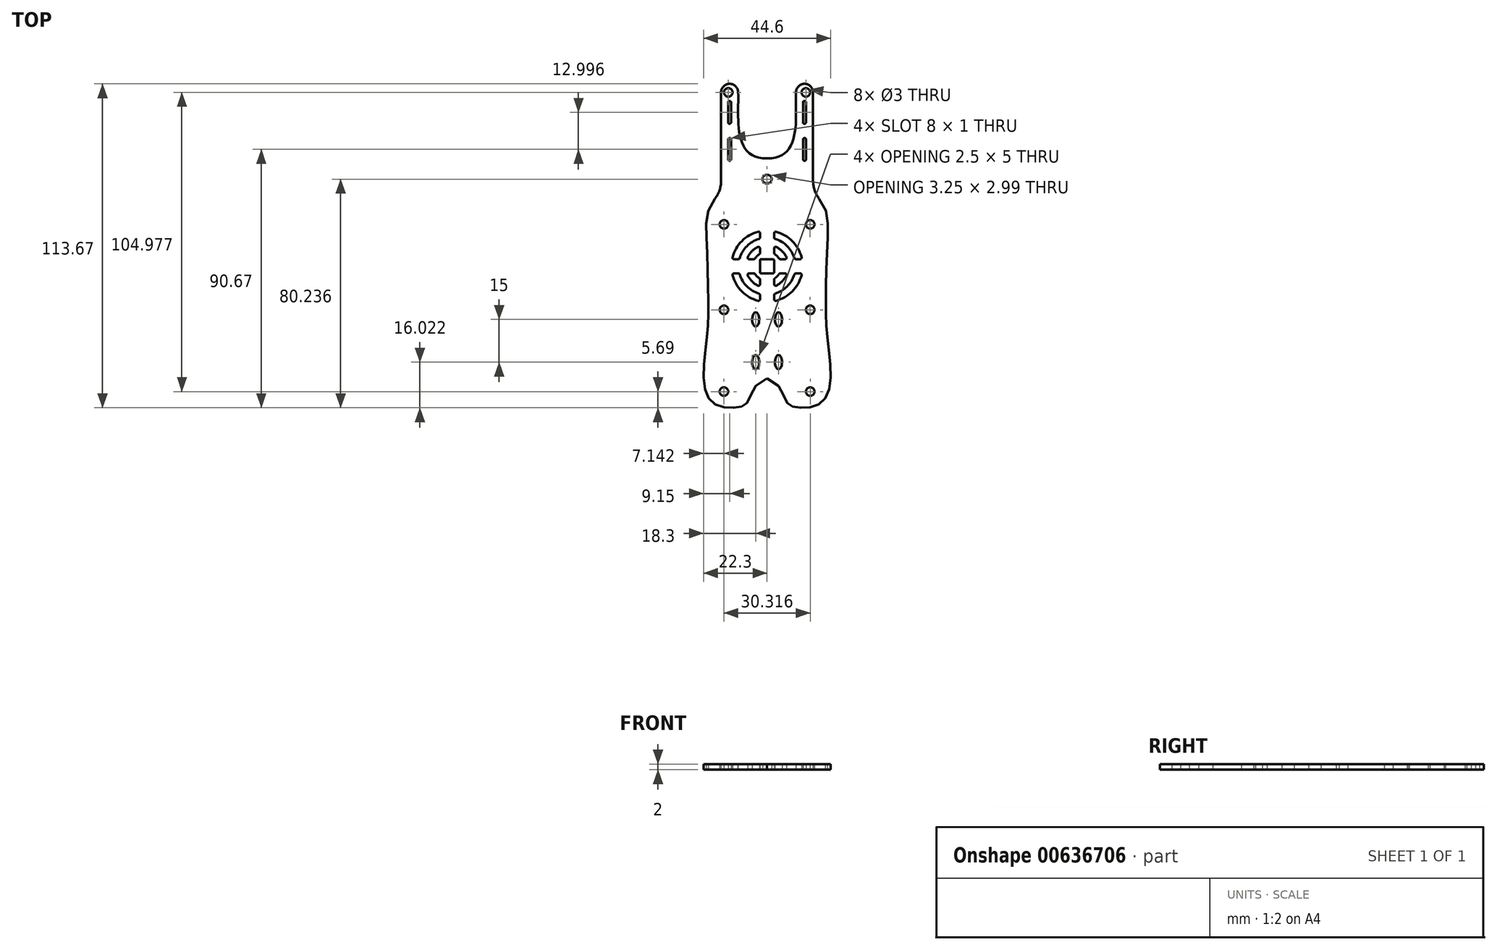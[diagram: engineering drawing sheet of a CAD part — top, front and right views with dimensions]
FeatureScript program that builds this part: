
annotation { "Feature Type Name" : "Feature", "Feature Type Description" : "" }
export const myFeature = defineFeature(function(context is Context, id is Id, definition is map)
    precondition{}
    {
        {
            var Q0;
            Q0=qCreatedBy(makeId("Top.planeOp"),FACE);
            var sketch = newSketch(context, id + "F0", { "sketchPlane" : qUnion([Q0])});
            skCircle(sketch, "E0", {"center": v(15.13, 14.7) * mm, "radius": 1.5 * mm});
            skCircle(sketch, "E1.MirrorC", {"center": v(15.13, -15.3) * mm, "radius": 1.5 * mm});
            skLineSegment(sketch, "E2", {"start": v(16.15, 29.9) * mm, "end": v(16.15, 61) * mm});
            skPoint(sketch, "E3.visualSharp", {"position": v(16.15, 66) * mm});
            skArc(sketch, "E3.filletArc", {"start": v(16.15, 61) * mm, "mid": v(15.24, 63.16) * mm, "end": v(13.06, 64) * mm});
            skArc(sketch, "E4", {"start": v(13.65, 57.5) * mm, "mid": v(13.11, 58) * mm, "end": v(12.65, 57.44) * mm});
            skArc(sketch, "E5", {"start": v(12.65, 37.58) * mm, "mid": v(13.11, 37.01) * mm, "end": v(13.65, 37.5) * mm});
            skLineSegment(sketch, "E6", {"start": v(13.65, 57.5) * mm, "end": v(13.65, 50.5) * mm});
            skLineSegment(sketch, "E7", {"start": v(12.65, 57.57) * mm, "end": v(12.65, 50.44) * mm});
            skPoint(sketch, "E8.visualSharp", {"position": v(8.63, 59.12) * mm});
            skPoint(sketch, "E9.visualSharp", {"position": v(8.63, 31.4) * mm});
            skCircle(sketch, "E10.MirrorC", {"center": v(13.63, 61) * mm, "radius": 1.5 * mm});
            skArc(sketch, "E11", {"start": v(12.65, 50.57) * mm, "mid": v(13.11, 50) * mm, "end": v(13.65, 50.5) * mm});
            skArc(sketch, "E12", {"start": v(13.65, 44.5) * mm, "mid": v(13.11, 45) * mm, "end": v(12.65, 44.44) * mm});
            skLineSegment(sketch, "E13.trimOffspring", {"start": v(12.65, 44.58) * mm, "end": v(12.65, 37.44) * mm});
            skLineSegment(sketch, "E14.trimOffspring", {"start": v(13.65, 44.5) * mm, "end": v(13.65, 37.5) * mm});
            skCircle(sketch, "E15", {"center": v(0.13, 30.58) * mm, "radius": 1.5 * mm});
            skCircle(sketch, "E16", {"center": v(15.16, -43.97) * mm, "radius": 1.5 * mm});
            skArc(sketch, "E17", {"start": v(13.06, 64) * mm, "mid": v(11, 63.1) * mm, "end": v(10.15, 61) * mm});
            skFitSpline(sketch, "E18", {"points": [v(10.15, 61) * mm, v(0, 37.84) * mm], "startDerivative": vector(-1.26, -21.95) * mm, "endDerivative": vector(-37.96, 1.2) * mm});
            skFitSpline(sketch, "E19", {"points": [v(16.15, 26) * mm, v(21.25, 10.3) * mm, v(20.6, -12.8) * mm, v(21.22, -25.83) * mm, v(22.05, -41.9) * mm, v(17.96, -48.52) * mm, v(10.33, -49.5) * mm, v(6.8, -47.51) * mm, v(0, -39.35) * mm], "startDerivative": vector(112.4, -103.66) * mm, "endDerivative": vector(-131.84, 47.57) * mm});
            skArc(sketch, "E20.MirrorCS", {"start": v(-12.65, 37.58) * mm, "mid": v(-13.11, 37.01) * mm, "end": v(-13.65, 37.5) * mm});
            skArc(sketch, "E21.MirrorCS", {"start": v(-12.65, 50.57) * mm, "mid": v(-13.11, 50) * mm, "end": v(-13.65, 50.5) * mm});
            skArc(sketch, "E22.MirrorCS", {"start": v(-13.65, 57.5) * mm, "mid": v(-13.11, 58) * mm, "end": v(-12.65, 57.44) * mm});
            skArc(sketch, "E23.MirrorCS", {"start": v(-13.65, 44.5) * mm, "mid": v(-13.11, 45) * mm, "end": v(-12.65, 44.44) * mm});
            skLineSegment(sketch, "E24.MirrorCS", {"start": v(-13.65, 57.5) * mm, "end": v(-13.65, 50.5) * mm});
            skCircle(sketch, "E25.MirrorC", {"center": v(-13.63, 61) * mm, "radius": 1.5 * mm});
            skLineSegment(sketch, "E26.MirrorCS", {"start": v(-12.65, 57.57) * mm, "end": v(-12.65, 50.44) * mm});
            skArc(sketch, "E27.MirrorCS", {"start": v(-16.15, 61) * mm, "mid": v(-15.24, 63.16) * mm, "end": v(-13.06, 64) * mm});
            skCircle(sketch, "E28.MirrorC", {"center": v(-0.13, 30.58) * mm, "radius": 1.5 * mm});
            skCircle(sketch, "E29.MirrorC", {"center": v(-15.16, -43.97) * mm, "radius": 1.5 * mm});
            skCircle(sketch, "E30.MirrorC", {"center": v(-15.13, -15.3) * mm, "radius": 1.5 * mm});
            skLineSegment(sketch, "E31.MirrorCS", {"start": v(-13.65, 44.5) * mm, "end": v(-13.65, 37.5) * mm});
            skCircle(sketch, "E32.MirrorC", {"center": v(-15.13, 14.7) * mm, "radius": 1.5 * mm});
            skLineSegment(sketch, "E33.MirrorCS", {"start": v(-16.15, 29.9) * mm, "end": v(-16.15, 61) * mm});
            skLineSegment(sketch, "E34.MirrorCS", {"start": v(-12.65, 44.58) * mm, "end": v(-12.65, 37.44) * mm});
            skArc(sketch, "E35.MirrorCS", {"start": v(-13.06, 64) * mm, "mid": v(-11, 63.1) * mm, "end": v(-10.15, 61) * mm});
            skPoint(sketch, "E36.MirrorP", {"position": v(-16.15, 66) * mm});
            skPoint(sketch, "E37.MirrorP", {"position": v(-8.63, 31.4) * mm});
            skFitSpline(sketch, "E38.MirrorCS", {"points": [v(-16.15, 26) * mm, v(-21.25, 10.3) * mm, v(-20.6, -12.8) * mm, v(-21.22, -25.83) * mm, v(-22.05, -41.9) * mm, v(-17.96, -48.52) * mm, v(-10.33, -49.5) * mm, v(-6.8, -47.51) * mm, v(0, -39.35) * mm], "startDerivative": vector(-112.4, -103.66) * mm, "endDerivative": vector(131.84, 47.57) * mm});
            skFitSpline(sketch, "E39.MirrorCS", {"points": [v(-10.15, 61) * mm, v(0, 37.84) * mm], "startDerivative": vector(1.26, -21.95) * mm, "endDerivative": vector(37.96, 1.2) * mm});
            skPoint(sketch, "E40.MirrorP", {"position": v(-8.63, 59.12) * mm});
            skArc(sketch, "E41.filletArc", {"start": v(-18.3, 23.7) * mm, "mid": v(-16.7, 26.62) * mm, "end": v(-16.15, 29.9) * mm});
            skArc(sketch, "E42.filletArc", {"start": v(16.15, 29.9) * mm, "mid": v(16.7, 26.62) * mm, "end": v(18.3, 23.7) * mm});
            skEllipse(sketch, "E43", {"center": v(-4, -33.64) * mm, "majorRadius": 2.5 * mm, "minorRadius": 1.25 * mm, "majorAxis": v(0, -1)});
            skEllipse(sketch, "E44", {"center": v(-4, -18.64) * mm, "majorRadius": 2.5 * mm, "minorRadius": 1.25 * mm, "majorAxis": v(0, -1)});
            skArc(sketch, "E45", {"start": v(-2.72, 4.2) * mm, "mid": v(-3.54, 3.54) * mm, "end": v(-4.2, 2.72) * mm});
            skArc(sketch, "E46", {"start": v(-3.2, 6.78) * mm, "mid": v(-5.3, 5.3) * mm, "end": v(-6.78, 3.2) * mm});
            skArc(sketch, "E47", {"start": v(-2.85, 9.58) * mm, "mid": v(-7.07, 7.07) * mm, "end": v(-9.58, 2.85) * mm});
            skArc(sketch, "E48", {"start": v(-3.12, 12.1) * mm, "mid": v(-8.84, 8.84) * mm, "end": v(-12.1, 3.12) * mm});
            skLineSegment(sketch, "E49.left", {"start": v(2.5, -11.63) * mm, "end": v(2.5, -10.06) * mm});
            skLineSegment(sketch, "E49.right", {"start": v(-2.5, -11.63) * mm, "end": v(-2.5, -10.06) * mm});
            skLineSegment(sketch, "E50.bottom", {"start": v(11.63, -2.5) * mm, "end": v(10.06, -2.5) * mm});
            skLineSegment(sketch, "E50.top", {"start": v(11.63, 2.5) * mm, "end": v(10.06, 2.5) * mm});
            skArc(sketch, "E51.trimOffspring", {"start": v(2.72, -4.2) * mm, "mid": v(3.54, -3.54) * mm, "end": v(4.2, -2.72) * mm});
            skArc(sketch, "E52.trimOffspring", {"start": v(3.2, -6.78) * mm, "mid": v(5.3, -5.3) * mm, "end": v(6.78, -3.2) * mm});
            skArc(sketch, "E53.trimOffspring", {"start": v(2.85, -9.58) * mm, "mid": v(7.07, -7.07) * mm, "end": v(9.58, -2.85) * mm});
            skArc(sketch, "E54.trimOffspring", {"start": v(3.12, -12.1) * mm, "mid": v(8.84, -8.84) * mm, "end": v(12.1, -3.12) * mm});
            skPoint(sketch, "E55.orphan", {"position": v(-17.4, -2.5) * mm});
            skPoint(sketch, "E56.orphan", {"position": v(-17.4, 2.5) * mm});
            skArc(sketch, "E57.trimOffspring", {"start": v(-12.1, -3.12) * mm, "mid": v(-8.84, -8.84) * mm, "end": v(-3.12, -12.1) * mm});
            skArc(sketch, "E58.trimOffspring", {"start": v(-9.58, -2.85) * mm, "mid": v(-7.07, -7.07) * mm, "end": v(-2.85, -9.58) * mm});
            skArc(sketch, "E59.trimOffspring", {"start": v(-6.78, -3.2) * mm, "mid": v(-5.3, -5.3) * mm, "end": v(-3.2, -6.78) * mm});
            skArc(sketch, "E60.trimOffspring", {"start": v(-4.2, -2.72) * mm, "mid": v(-3.54, -3.54) * mm, "end": v(-2.72, -4.2) * mm});
            skLineSegment(sketch, "E61.trimOffspring", {"start": v(-4.6, -2.5) * mm, "end": v(-6.34, -2.5) * mm});
            skLineSegment(sketch, "E62.trimOffspring", {"start": v(-2.5, -2) * mm, "end": v(-2.5, 2) * mm});
            skLineSegment(sketch, "E63.trimOffspring", {"start": v(2.5, -2) * mm, "end": v(2.5, 2) * mm});
            skLineSegment(sketch, "E64.trimOffspring", {"start": v(2, -2.5) * mm, "end": v(-2, -2.5) * mm});
            skLineSegment(sketch, "E65.trimOffspring", {"start": v(2, 2.5) * mm, "end": v(-2, 2.5) * mm});
            skLineSegment(sketch, "E66.trimOffspring", {"start": v(2.5, 4.6) * mm, "end": v(2.5, 6.34) * mm});
            skLineSegment(sketch, "E67.trimOffspring", {"start": v(-2.5, 4.6) * mm, "end": v(-2.5, 6.34) * mm});
            skLineSegment(sketch, "E68.trimOffspring", {"start": v(-4.6, 2.5) * mm, "end": v(-6.34, 2.5) * mm});
            skPoint(sketch, "E69.orphan", {"position": v(-2.5, 16.27) * mm});
            skPoint(sketch, "E70.orphan", {"position": v(2.5, 16.27) * mm});
            skPoint(sketch, "E50.left.end.orphan", {"position": v(17.4, 2.5) * mm});
            skPoint(sketch, "E71.orphan", {"position": v(17.4, -2.5) * mm});
            skPoint(sketch, "E72.orphan", {"position": v(2.5, -16.27) * mm});
            skPoint(sketch, "E73.orphan", {"position": v(-2.5, -16.27) * mm});
            skArc(sketch, "E74.trimOffspring", {"start": v(4.2, 2.72) * mm, "mid": v(3.54, 3.54) * mm, "end": v(2.72, 4.2) * mm});
            skArc(sketch, "E75.trimOffspring", {"start": v(6.78, 3.2) * mm, "mid": v(5.3, 5.3) * mm, "end": v(3.2, 6.78) * mm});
            skArc(sketch, "E76.trimOffspring", {"start": v(9.58, 2.85) * mm, "mid": v(7.07, 7.07) * mm, "end": v(2.85, 9.58) * mm});
            skArc(sketch, "E77.trimOffspring", {"start": v(12.1, 3.12) * mm, "mid": v(8.84, 8.84) * mm, "end": v(3.12, 12.1) * mm});
            skLineSegment(sketch, "E78.trimOffspring", {"start": v(2.5, 10.06) * mm, "end": v(2.5, 11.63) * mm});
            skLineSegment(sketch, "E79.trimOffspring", {"start": v(6.34, 2.5) * mm, "end": v(4.6, 2.5) * mm});
            skLineSegment(sketch, "E80.trimOffspring", {"start": v(-2.5, 10.06) * mm, "end": v(-2.5, 11.63) * mm});
            skLineSegment(sketch, "E81.trimOffspring", {"start": v(-10.06, 2.5) * mm, "end": v(-11.63, 2.5) * mm});
            skLineSegment(sketch, "E82.trimOffspring", {"start": v(-2.5, -6.34) * mm, "end": v(-2.5, -4.6) * mm});
            skLineSegment(sketch, "E83.trimOffspring", {"start": v(2.5, -6.34) * mm, "end": v(2.5, -4.6) * mm});
            skLineSegment(sketch, "E84.trimOffspring", {"start": v(6.34, -2.5) * mm, "end": v(4.6, -2.5) * mm});
            skPoint(sketch, "E85.visualSharp", {"position": v(-9.68, 2.5) * mm});
            skArc(sketch, "E85.filletArc", {"start": v(-10.06, 2.5) * mm, "mid": v(-9.76, 2.6) * mm, "end": v(-9.58, 2.85) * mm});
            skPoint(sketch, "E86.visualSharp", {"position": v(-12.25, 2.5) * mm});
            skArc(sketch, "E86.filletArc", {"start": v(-12.1, 3.12) * mm, "mid": v(-12.02, 2.7) * mm, "end": v(-11.63, 2.5) * mm});
            skPoint(sketch, "E87.visualSharp", {"position": v(-2.5, 12.25) * mm});
            skArc(sketch, "E87.filletArc", {"start": v(-2.5, 11.63) * mm, "mid": v(-2.7, 12.02) * mm, "end": v(-3.12, 12.1) * mm});
            skPoint(sketch, "E88.visualSharp", {"position": v(-2.5, 9.68) * mm});
            skArc(sketch, "E88.filletArc", {"start": v(-2.85, 9.58) * mm, "mid": v(-2.6, 9.76) * mm, "end": v(-2.5, 10.06) * mm});
            skPoint(sketch, "E89.visualSharp", {"position": v(-2.5, 4.33) * mm});
            skArc(sketch, "E89.filletArc", {"start": v(-2.72, 4.2) * mm, "mid": v(-2.56, 4.37) * mm, "end": v(-2.5, 4.6) * mm});
            skPoint(sketch, "E90.visualSharp", {"position": v(-4.33, 2.5) * mm});
            skArc(sketch, "E90.filletArc", {"start": v(-4.6, 2.5) * mm, "mid": v(-4.37, 2.56) * mm, "end": v(-4.2, 2.72) * mm});
            skPoint(sketch, "E91.visualSharp", {"position": v(-7.07, 2.5) * mm});
            skArc(sketch, "E91.filletArc", {"start": v(-6.78, 3.2) * mm, "mid": v(-6.75, 2.73) * mm, "end": v(-6.34, 2.5) * mm});
            skPoint(sketch, "E92.visualSharp", {"position": v(2.5, 12.25) * mm});
            skArc(sketch, "E92.filletArc", {"start": v(3.12, 12.1) * mm, "mid": v(2.7, 12.02) * mm, "end": v(2.5, 11.63) * mm});
            skPoint(sketch, "E93.visualSharp", {"position": v(2.5, 4.33) * mm});
            skArc(sketch, "E93.filletArc", {"start": v(2.5, 4.6) * mm, "mid": v(2.56, 4.37) * mm, "end": v(2.72, 4.2) * mm});
            skPoint(sketch, "E94.visualSharp", {"position": v(2.5, 7.07) * mm});
            skArc(sketch, "E94.filletArc", {"start": v(3.2, 6.78) * mm, "mid": v(2.73, 6.75) * mm, "end": v(2.5, 6.34) * mm});
            skPoint(sketch, "E95.visualSharp", {"position": v(2.5, 9.68) * mm});
            skArc(sketch, "E95.filletArc", {"start": v(2.5, 10.06) * mm, "mid": v(2.6, 9.76) * mm, "end": v(2.85, 9.58) * mm});
            skPoint(sketch, "E96.visualSharp", {"position": v(7.07, 2.5) * mm});
            skArc(sketch, "E96.filletArc", {"start": v(6.34, 2.5) * mm, "mid": v(6.75, 2.73) * mm, "end": v(6.78, 3.2) * mm});
            skPoint(sketch, "E97.visualSharp", {"position": v(9.68, 2.5) * mm});
            skArc(sketch, "E97.filletArc", {"start": v(9.58, 2.85) * mm, "mid": v(9.76, 2.6) * mm, "end": v(10.06, 2.5) * mm});
            skPoint(sketch, "E98.visualSharp", {"position": v(12.25, 2.5) * mm});
            skArc(sketch, "E98.filletArc", {"start": v(11.63, 2.5) * mm, "mid": v(12.02, 2.7) * mm, "end": v(12.1, 3.12) * mm});
            skPoint(sketch, "E99.visualSharp", {"position": v(4.33, 2.5) * mm});
            skArc(sketch, "E99.filletArc", {"start": v(4.2, 2.72) * mm, "mid": v(4.37, 2.56) * mm, "end": v(4.6, 2.5) * mm});
            skPoint(sketch, "E100.visualSharp", {"position": v(4.33, -2.5) * mm});
            skArc(sketch, "E100.filletArc", {"start": v(4.6, -2.5) * mm, "mid": v(4.37, -2.56) * mm, "end": v(4.2, -2.72) * mm});
            skPoint(sketch, "E101.visualSharp", {"position": v(2.5, -2.5) * mm});
            skArc(sketch, "E101.filletArc", {"start": v(2, -2.5) * mm, "mid": v(2.36, -2.36) * mm, "end": v(2.5, -2) * mm});
            skPoint(sketch, "E102.visualSharp", {"position": v(-2.5, -2.5) * mm});
            skArc(sketch, "E102.filletArc", {"start": v(-2.5, -2) * mm, "mid": v(-2.36, -2.36) * mm, "end": v(-2, -2.5) * mm});
            skPoint(sketch, "E103.visualSharp", {"position": v(2.5, 2.5) * mm});
            skArc(sketch, "E103.filletArc", {"start": v(2.5, 2) * mm, "mid": v(2.36, 2.36) * mm, "end": v(2, 2.5) * mm});
            skPoint(sketch, "E104.visualSharp", {"position": v(-4.33, -2.5) * mm});
            skArc(sketch, "E104.filletArc", {"start": v(-4.2, -2.72) * mm, "mid": v(-4.37, -2.56) * mm, "end": v(-4.6, -2.5) * mm});
            skPoint(sketch, "E105.visualSharp", {"position": v(-2.5, -7.07) * mm});
            skArc(sketch, "E105.filletArc", {"start": v(-3.2, -6.78) * mm, "mid": v(-2.73, -6.75) * mm, "end": v(-2.5, -6.34) * mm});
            skLineSegment(sketch, "E106.trimOffspring", {"start": v(-10.06, -2.5) * mm, "end": v(-11.63, -2.5) * mm});
            skPoint(sketch, "E107.visualSharp", {"position": v(-7.07, -2.5) * mm});
            skArc(sketch, "E107.filletArc", {"start": v(-6.34, -2.5) * mm, "mid": v(-6.75, -2.73) * mm, "end": v(-6.78, -3.2) * mm});
            skPoint(sketch, "E108.visualSharp", {"position": v(-2.5, -4.33) * mm});
            skArc(sketch, "E108.filletArc", {"start": v(-2.5, -4.6) * mm, "mid": v(-2.56, -4.37) * mm, "end": v(-2.72, -4.2) * mm});
            skPoint(sketch, "E109.visualSharp", {"position": v(2.5, -4.33) * mm});
            skArc(sketch, "E109.filletArc", {"start": v(2.72, -4.2) * mm, "mid": v(2.56, -4.37) * mm, "end": v(2.5, -4.6) * mm});
            skPoint(sketch, "E110.visualSharp", {"position": v(2.5, -7.07) * mm});
            skArc(sketch, "E110.filletArc", {"start": v(2.5, -6.34) * mm, "mid": v(2.73, -6.75) * mm, "end": v(3.2, -6.78) * mm});
            skPoint(sketch, "E111.visualSharp", {"position": v(9.68, -2.5) * mm});
            skArc(sketch, "E111.filletArc", {"start": v(10.06, -2.5) * mm, "mid": v(9.76, -2.6) * mm, "end": v(9.58, -2.85) * mm});
            skPoint(sketch, "E112.visualSharp", {"position": v(12.25, -2.5) * mm});
            skArc(sketch, "E112.filletArc", {"start": v(12.1, -3.12) * mm, "mid": v(12.02, -2.7) * mm, "end": v(11.63, -2.5) * mm});
            skPoint(sketch, "E113.visualSharp", {"position": v(2.5, -12.25) * mm});
            skArc(sketch, "E113.filletArc", {"start": v(2.5, -11.63) * mm, "mid": v(2.7, -12.02) * mm, "end": v(3.12, -12.1) * mm});
            skPoint(sketch, "E114.visualSharp", {"position": v(-2.5, -9.68) * mm});
            skArc(sketch, "E114.filletArc", {"start": v(-2.5, -10.06) * mm, "mid": v(-2.6, -9.76) * mm, "end": v(-2.85, -9.58) * mm});
            skPoint(sketch, "E115.visualSharp", {"position": v(-12.25, -2.5) * mm});
            skArc(sketch, "E115.filletArc", {"start": v(-11.63, -2.5) * mm, "mid": v(-12.02, -2.7) * mm, "end": v(-12.1, -3.12) * mm});
            skPoint(sketch, "E116.visualSharp", {"position": v(-2.5, -12.25) * mm});
            skArc(sketch, "E116.filletArc", {"start": v(-3.12, -12.1) * mm, "mid": v(-2.7, -12.02) * mm, "end": v(-2.5, -11.63) * mm});
            skPoint(sketch, "E117.visualSharp", {"position": v(-9.68, -2.5) * mm});
            skArc(sketch, "E117.filletArc", {"start": v(-9.58, -2.85) * mm, "mid": v(-9.76, -2.6) * mm, "end": v(-10.06, -2.5) * mm});
            skPoint(sketch, "E118.visualSharp", {"position": v(-2.5, 2.5) * mm});
            skArc(sketch, "E118.filletArc", {"start": v(-2, 2.5) * mm, "mid": v(-2.36, 2.36) * mm, "end": v(-2.5, 2) * mm});
            skPoint(sketch, "E119.visualSharp", {"position": v(-2.5, 7.07) * mm});
            skArc(sketch, "E119.filletArc", {"start": v(-2.5, 6.34) * mm, "mid": v(-2.73, 6.75) * mm, "end": v(-3.2, 6.78) * mm});
            skPoint(sketch, "E120.visualSharp", {"position": v(7.07, -2.5) * mm});
            skArc(sketch, "E120.filletArc", {"start": v(6.78, -3.2) * mm, "mid": v(6.75, -2.73) * mm, "end": v(6.34, -2.5) * mm});
            skPoint(sketch, "E121.visualSharp", {"position": v(2.5, -9.68) * mm});
            skArc(sketch, "E121.filletArc", {"start": v(2.85, -9.58) * mm, "mid": v(2.6, -9.76) * mm, "end": v(2.5, -10.06) * mm});
            skEllipse(sketch, "E122.MirrorC", {"center": v(4, -18.64) * mm, "majorRadius": 2.5 * mm, "minorRadius": 1.25 * mm, "majorAxis": v(0, -1)});
            skEllipse(sketch, "E123.MirrorC", {"center": v(4, -33.64) * mm, "majorRadius": 2.5 * mm, "minorRadius": 1.25 * mm, "majorAxis": v(0, -1)});
            skSolve(sketch);
        }
        {
            var Q0;
            Q0=makeQuery(id+"F0.imprint","IMPRINT",FACE,{"disambiguationData":[TD([[makeQuery(id+"F0.imprint","IMPRINT",EDGE,{"derivedFrom":sQuery(id+"F0.wireOp",EDGE,"E0")}),-1.0]])]});
            extrude(context, id + "F1", {"entities" : qUnion([Q0]), "depth" : 2 * mm, "offsetDistance" : 25 * mm});
        }
        {
            var Q0;
            Q0=makeQuery(id+"F1.opExtrude","CAP_EDGE",EDGE,{"disambiguationData":[OSD([sQuery(id+"F0.wireOp",EDGE,"E48")])],"isStart":false});
            var Q1;
            Q1=makeQuery(id+"F1.opExtrude","CAP_EDGE",EDGE,{"disambiguationData":[OSD([sQuery(id+"F0.wireOp",EDGE,"E87.filletArc")])],"isStart":false});
            var Q2;
            Q2=makeQuery(id+"F1.opExtrude","CAP_EDGE",EDGE,{"disambiguationData":[OSD([sQuery(id+"F0.wireOp",EDGE,"E46")])],"isStart":false});
            var Q3;
            Q3=makeQuery(id+"F1.opExtrude","CAP_EDGE",EDGE,{"disambiguationData":[OSD([sQuery(id+"F0.wireOp",EDGE,"E58.trimOffspring")])],"isStart":false});
            var Q4;
            Q4=makeQuery(id+"F1.opExtrude","CAP_EDGE",EDGE,{"disambiguationData":[OSD([sQuery(id+"F0.wireOp",EDGE,"E60.trimOffspring")])],"isStart":false});
            var Q5;
            Q5=makeQuery(id+"F1.opExtrude","CAP_EDGE",EDGE,{"disambiguationData":[OSD([sQuery(id+"F0.wireOp",EDGE,"E65.trimOffspring")])],"isStart":false});
            var Q6;
            Q6=makeQuery(id+"F1.opExtrude","CAP_EDGE",EDGE,{"disambiguationData":[OSD([sQuery(id+"F0.wireOp",EDGE,"E75.trimOffspring")])],"isStart":false});
            var Q7;
            Q7=makeQuery(id+"F1.opExtrude","CAP_EDGE",EDGE,{"disambiguationData":[OSD([sQuery(id+"F0.wireOp",EDGE,"E77.trimOffspring")])],"isStart":false});
            var Q8;
            Q8=makeQuery(id+"F1.opExtrude","CAP_EDGE",EDGE,{"disambiguationData":[OSD([sQuery(id+"F0.wireOp",EDGE,"E52.trimOffspring")])],"isStart":false});
            var Q9;
            Q9=makeQuery(id+"F1.opExtrude","CAP_EDGE",EDGE,{"disambiguationData":[OSD([sQuery(id+"F0.wireOp",EDGE,"E54.trimOffspring")])],"isStart":false});
            fillet(context, id + "F2", {"entities" : qUnion([Q0, Q1, Q2, Q3, Q4, Q5, Q6, Q7, Q8, Q9]), "radius" : 0.5 * mm, "tangentPropagation" : true, "allowEdgeOverflow" : false});
        }
    });
